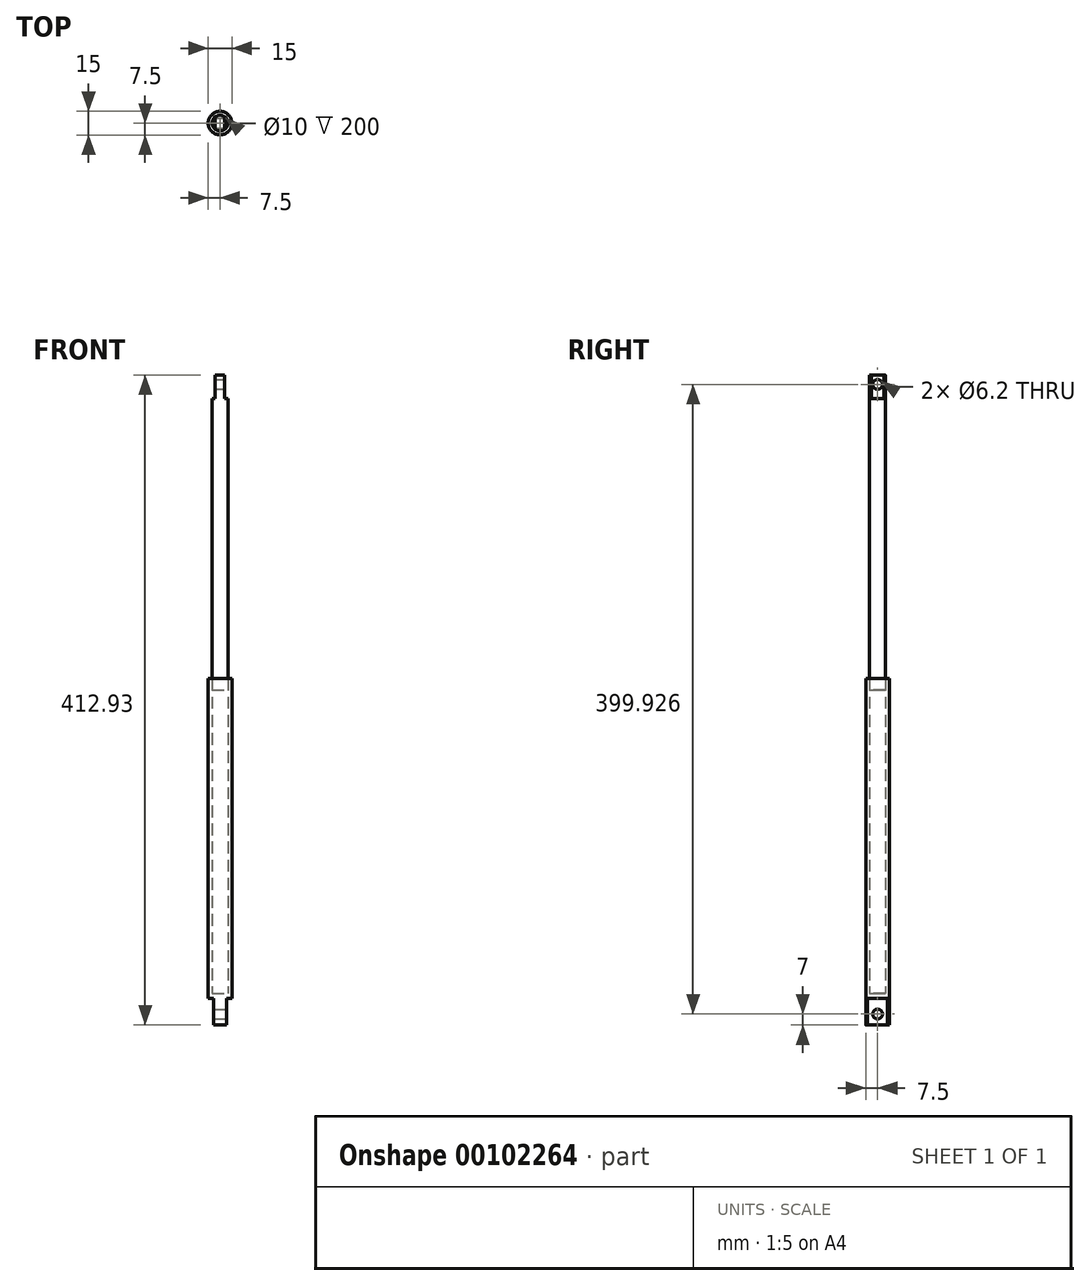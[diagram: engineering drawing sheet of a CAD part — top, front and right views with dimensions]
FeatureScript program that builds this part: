
annotation { "Feature Type Name" : "Feature", "Feature Type Description" : "" }
export const myFeature = defineFeature(function(context is Context, id is Id, definition is map)
    precondition{}
    {
        {
            var Q0;
            Q0=qCreatedBy(makeId("Front.planeOp"),FACE);
            var sketch = newSketch(context, id + "F0", { "sketchPlane" : qUnion([Q0])});
            skLineSegment(sketch, "E0.bottom", {"start": v(0, 0) * mm, "end": v(-7.5, 0) * mm});
            skLineSegment(sketch, "E0.top", {"start": v(-5, 220) * mm, "end": v(-7.5, 220) * mm});
            skLineSegment(sketch, "E0.left", {"start": v(0, 0) * mm, "end": v(0, 20) * mm});
            skLineSegment(sketch, "E0.right", {"start": v(-7.5, 0) * mm, "end": v(-7.5, 220) * mm});
            skLineSegment(sketch, "E1.bottom", {"start": v(0, 20) * mm, "end": v(-5, 20) * mm});
            skLineSegment(sketch, "E1.right", {"start": v(-5, 20) * mm, "end": v(-5, 220) * mm});
            skLineSegment(sketch, "E2", {"start": v(0, -22.33) * mm, "end": v(0, 450.18) * mm, "construction": true});
            skSolve(sketch);
        }
        {
            var Q0;
            Q0 = qSketchRegion(id + "F0", true);
            var Q1;
            Q1=sQuery(id+"F0.wireOp",EDGE,"E2");
            revolve(context, id + "F1", {"entities" : qUnion([Q0]), "axis" : qUnion([Q1]), "revolveType" : RevolveType.FULL});
        }
        {
            var Q0;
            Q0=qCreatedBy(makeId("Front.planeOp"),FACE);
            var sketch = newSketch(context, id + "F2", { "sketchPlane" : qUnion([Q0])});
            skLineSegment(sketch, "E3", {"start": v(-4, 0) * mm, "end": v(-4, 17) * mm});
            skLineSegment(sketch, "E4", {"start": v(-4, 17) * mm, "end": v(-14.87, 17) * mm});
            skLineSegment(sketch, "E5", {"start": v(-14.87, 17) * mm, "end": v(-14.87, 0) * mm});
            skLineSegment(sketch, "E6", {"start": v(-14.87, 0) * mm, "end": v(-4, 0) * mm});
            skLineSegment(sketch, "E7.MirrorCS", {"start": v(14.87, 0) * mm, "end": v(4, 0) * mm});
            skLineSegment(sketch, "E8.MirrorCS", {"start": v(14.87, 17) * mm, "end": v(14.87, 0) * mm});
            skLineSegment(sketch, "E9.MirrorCS", {"start": v(4, 0) * mm, "end": v(4, 17) * mm});
            skLineSegment(sketch, "E10.MirrorCS", {"start": v(4, 17) * mm, "end": v(14.87, 17) * mm});
            skSolve(sketch);
        }
        {
            var Q0;
            Q0 = qSketchRegion(id + "F2", true);
            extrude(context, id + "F3", {"entities" : qUnion([Q0]), "operationType" : NewBodyOperationType.REMOVE, "endBound" : BoundingType.SYMMETRIC, "oppositeDirection" : true, "depth" : 25 * mm});
        }
        {
            var Q0;
            Q0=qCreatedBy(makeId("Front.planeOp"),FACE);
            var sketch = newSketch(context, id + "F4", { "sketchPlane" : qUnion([Q0])});
            skLineSegment(sketch, "E11.bottom", {"start": v(0, 212.93) * mm, "end": v(-5, 212.93) * mm});
            skLineSegment(sketch, "E11.top", {"start": v(0, 412.93) * mm, "end": v(-5, 412.93) * mm});
            skLineSegment(sketch, "E11.left", {"start": v(0, 212.93) * mm, "end": v(0, 412.93) * mm});
            skLineSegment(sketch, "E11.right", {"start": v(-5, 212.93) * mm, "end": v(-5, 412.93) * mm});
            skSolve(sketch);
        }
        {
            var Q0;
            Q0 = qSketchRegion(id + "F4", true);
            var Q1;
            Q1=sQuery(id+"F0.wireOp",EDGE,"E2");
            revolve(context, id + "F5", {"entities" : qUnion([Q0]), "axis" : qUnion([Q1]), "revolveType" : RevolveType.FULL});
        }
        {
            var Q0;
            Q0=makeQuery(id+"F3.boolean.opBoolean","COPY",FACE,{"derivedFrom":makeQuery(id+"F3.opExtrude","SWEPT_FACE",FACE,{"disambiguationData":[OSD([sQuery(id+"F2.wireOp",EDGE,"E9.MirrorCS")])]})});
            var sketch = newSketch(context, id + "F6", { "sketchPlane" : qUnion([Q0])});
            skCircle(sketch, "E12", {"center": v(0, 7) * mm, "radius": 3.1 * mm});
            skSolve(sketch);
        }
        {
            var Q0;
            Q0 = qSketchRegion(id + "F6", true);
            extrude(context, id + "F7", {"entities" : qUnion([Q0]), "operationType" : NewBodyOperationType.REMOVE, "endBound" : BoundingType.THROUGH_ALL, "oppositeDirection" : true, "depth" : 25 * mm});
        }
        {
            var Q0;
            Q0=qCreatedBy(makeId("Front.planeOp"),FACE);
            var sketch = newSketch(context, id + "F8", { "sketchPlane" : qUnion([Q0])});
            skLineSegment(sketch, "E13.right", {"start": v(-9.71, 412.93) * mm, "end": v(-9.71, 397.93) * mm});
            skLineSegment(sketch, "E14", {"start": v(-9.71, 397.93) * mm, "end": v(-3, 397.93) * mm});
            skLineSegment(sketch, "E15", {"start": v(-3, 397.93) * mm, "end": v(-3, 412.97) * mm});
            skLineSegment(sketch, "E16", {"start": v(-3, 412.97) * mm, "end": v(-9.71, 412.93) * mm});
            skLineSegment(sketch, "E17.MirrorCS", {"start": v(3, 397.93) * mm, "end": v(3, 412.97) * mm});
            skLineSegment(sketch, "E18.MirrorCS", {"start": v(3, 412.97) * mm, "end": v(9.71, 412.93) * mm});
            skLineSegment(sketch, "E19.MirrorCS", {"start": v(9.71, 412.93) * mm, "end": v(9.71, 397.93) * mm});
            skLineSegment(sketch, "E20.MirrorCS", {"start": v(9.71, 397.93) * mm, "end": v(3, 397.93) * mm});
            skSolve(sketch);
        }
        {
            var Q0;
            Q0 = qSketchRegion(id + "F8", true);
            extrude(context, id + "F9", {"entities" : qUnion([Q0]), "operationType" : NewBodyOperationType.REMOVE, "endBound" : BoundingType.SYMMETRIC, "oppositeDirection" : true, "depth" : 25 * mm});
        }
        {
            var Q0;
            Q0=makeQuery(id+"F9.boolean.opBoolean","COPY",FACE,{"derivedFrom":makeQuery(id+"F9.opExtrude","SWEPT_FACE",FACE,{"disambiguationData":[OSD([sQuery(id+"F8.wireOp",EDGE,"E17.MirrorCS")])]})});
            var sketch = newSketch(context, id + "F10", { "sketchPlane" : qUnion([Q0])});
            skCircle(sketch, "E21", {"center": v(0, 406.93) * mm, "radius": 3.1 * mm});
            skSolve(sketch);
        }
        {
            var Q0;
            Q0 = qSketchRegion(id + "F10", true);
            extrude(context, id + "F11", {"entities" : qUnion([Q0]), "operationType" : NewBodyOperationType.REMOVE, "endBound" : BoundingType.THROUGH_ALL, "oppositeDirection" : true, "depth" : 25 * mm});
        }
    });
